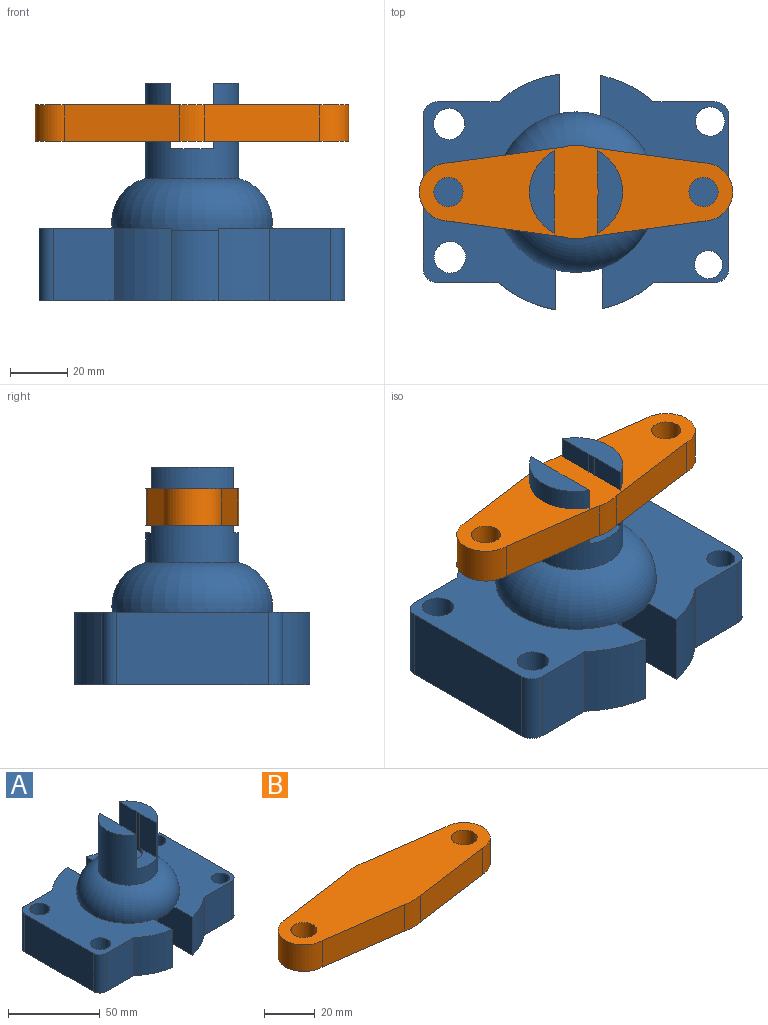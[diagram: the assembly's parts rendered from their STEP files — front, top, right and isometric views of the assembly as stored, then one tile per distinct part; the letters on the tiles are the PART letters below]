
ASSEMBLY  parts=2 mates=1
PART A: 41 faces, bbox 106.7x82.3x76 mm
  f0: cylinder r=16.26mm len=33.3mm, axis (0,0,-1), area 2673.6mm2, adj f1,f3,f4,f35,f36,f37,f38,f39
  f1: plane 28.73x8.64mm, normal (0,0,1), area 176.6mm2, adj f0,f2,f37,f38
  f2: cylinder r=7.73mm len=25.4mm, axis (0,0,1), area 240.8mm2, adj f1,f3,f34,f35,f36,f37,f38,f39
  f3: plane 28.73x8.64mm, normal (0,0,1), area 176.6mm2, adj f0,f2,f35,f40
  f4: torus R=12.12mm, axis (0,0,1), area 3484.4mm2, adj f0,f5,f6,f26,f27,f28,f29,f30
  f5: plane 16.11x14.36mm, normal (0,0,-1), area 191.3mm2, adj f4,f27,f29,f32
  f6: plane 14.3x13.99mm, normal (0,0,-1), area 168.9mm2, adj f4,f26,f30,f33
  f7: cylinder r=5.45mm len=25.4mm, axis (0,0,1), area 869.7mm2, adj f24,f31
  f8: cylinder r=5.51mm len=25.4mm, axis (0,0,1), area 879.2mm2, adj f24,f31
  f9: plane 25.4x21.08mm, normal (0,-1,0), area 535.4mm2, adj f10,f21,f24,f31
  f10: cylinder r=5.08mm len=25.4mm, axis (0,0,-1), area 202.7mm2, adj f9,f11,f24,f31
  f11: plane 52.88x25.4mm, normal (-1,0,0), area 1343.1mm2, adj f10,f12,f24,f31
  f12: cylinder r=5.08mm len=25.4mm, axis (0,0,1), area 202.7mm2, adj f11,f13,f24,f31
  f13: plane 25.4x21.08mm, normal (0,1,0), area 535.4mm2, adj f12,f23,f24,f31
  f14: cylinder r=4.87mm len=25.4mm, axis (0,0,1), area 777.9mm2, adj f24,f28
  f15: cylinder r=5.1mm len=25.4mm, axis (0,0,1), area 814.3mm2, adj f24,f28
  f16: plane 25.4x21.08mm, normal (0,1,0), area 535.4mm2, adj f17,f24,f25,f28
  f17: cylinder r=5.08mm len=25.4mm, axis (0,0,-1), area 202.7mm2, adj f16,f18,f24,f28
  f18: plane 52.88x25.4mm, normal (1,0,0), area 1343.1mm2, adj f17,f19,f24,f28
  f19: cylinder r=5.08mm len=25.4mm, axis (0,0,1), area 202.7mm2, adj f18,f20,f24,f28
  f20: plane 25.4x21.08mm, normal (0,-1,0), area 535.4mm2, adj f19,f22,f24,f28
  f21: cylinder r=41.62mm len=25.4mm, axis (0,0,-1), area 574.1mm2, adj f9,f24,f29,f31
  f22: cylinder r=41.62mm len=25.4mm, axis (0,0,-1), area 518.6mm2, adj f20,f24,f27,f28
  f23: cylinder r=41.62mm len=25.4mm, axis (0,0,-1), area 606.1mm2, adj f13,f24,f30,f31
  f24: plane 106.68x82.25mm, normal (0,0,-1), area 6325.7mm2, adj f7,f8,f9,f10,f11,f12,f13,f14
  f25: cylinder r=41.62mm len=25.4mm, axis (0,0,-1), area 533.4mm2, adj f16,f24,f26,f28
  f26: plane 26.91x25.4mm, normal (-1,0,0), area 675.1mm2, adj f4,f6,f24,f25,f28,f33
  f27: plane 27.16x25.4mm, normal (-1,0,0), area 681.3mm2, adj f4,f5,f22,f24,f28,f32
  f28: plane 81.34x44.78mm, normal (0,0,1), area 2102.4mm2, adj f4,f14,f15,f16,f17,f18,f19,f20
  f29: plane 26.35x25.4mm, normal (1,0,0), area 661.2mm2, adj f4,f5,f21,f24,f31,f32
  f30: plane 26.01x25.4mm, normal (1,0,0), area 652.8mm2, adj f4,f6,f23,f24,f31,f33
  f31: plane 82.25x47.6mm, normal (0,0,1), area 2139.9mm2, adj f4,f7,f8,f9,f10,f11,f12,f13
  f32: cylinder r=16.26mm len=24.74mm, axis (0,0,-1), area 418.5mm2, adj f5,f24,f27,f29
  f33: cylinder r=16.26mm len=24.74mm, axis (0,0,-1), area 368.1mm2, adj f6,f24,f26,f30
  f34: plane 15.47x15.47mm, normal (0,0,1), area 187.9mm2, adj f2
  f35: plane 22.96x13.04mm, normal (-1,0,0), area 299.4mm2, adj f0,f2,f3,f36
  f36: plane 15.24x14.93mm, normal (0,0,1), area 144.6mm2, adj f0,f2,f35,f37
  f37: plane 22.96x13.04mm, normal (1,0,0), area 299.4mm2, adj f0,f1,f2,f36
  f38: plane 22.96x13.04mm, normal (1,0,0), area 299.4mm2, adj f0,f1,f2,f39
  f39: plane 15.24x14.93mm, normal (0,0,1), area 144.6mm2, adj f0,f2,f38,f40
  f40: plane 22.96x13.04mm, normal (-1,0,0), area 299.4mm2, adj f0,f2,f3,f39
PART B: 12 faces, bbox 109.3x32.5x12.7 mm
  f0: plane 40.15x12.7mm, normal (-0.14,-0.99,0), area 514.7mm2, adj f1,f8,f10,f11
  f1: cylinder r=16.26mm len=12.7mm, axis (0,0,-1), area 111.2mm2, adj f0,f2,f10,f11
  f2: plane 40.15x12.7mm, normal (0.14,-0.99,0), area 514.7mm2, adj f1,f3,f10,f11
  f3: cylinder r=10.16mm len=20.32mm, axis (0,0,-1), area 405.4mm2, adj f2,f4,f10,f11
  f4: plane 40.15x12.7mm, normal (0.14,0.99,0), area 514.7mm2, adj f3,f5,f10,f11
  f5: cylinder r=16.26mm len=12.7mm, axis (0,0,-1), area 111.2mm2, adj f4,f6,f10,f11
  f6: plane 40.15x12.7mm, normal (-0.14,0.99,0), area 514.7mm2, adj f5,f8,f10,f11
  f7: cylinder r=5.08mm len=12.7mm, axis (0,0,-1), area 405.4mm2, adj f10,f11
  f8: cylinder r=10.16mm len=20.32mm, axis (0,0,-1), area 405.4mm2, adj f0,f6,f10,f11
  f9: cylinder r=5.08mm len=12.7mm, axis (0,0,-1), area 405.4mm2, adj f10,f11
  f10: plane 109.27x32.51mm, normal (0,0,1), area 2514.2mm2, adj f0,f1,f2,f3,f4,f5,f6,f7
  f11: plane 109.27x32.51mm, normal (0,0,-1), area 2514.2mm2, adj f0,f1,f2,f3,f4,f5,f6,f7
PLACE A at identity
PLACE B t=(0,0,55.7)mm
MATE fastened B.f1 <-> A.f0  axis (0,0,-1) through (0,0,55.7)mm
